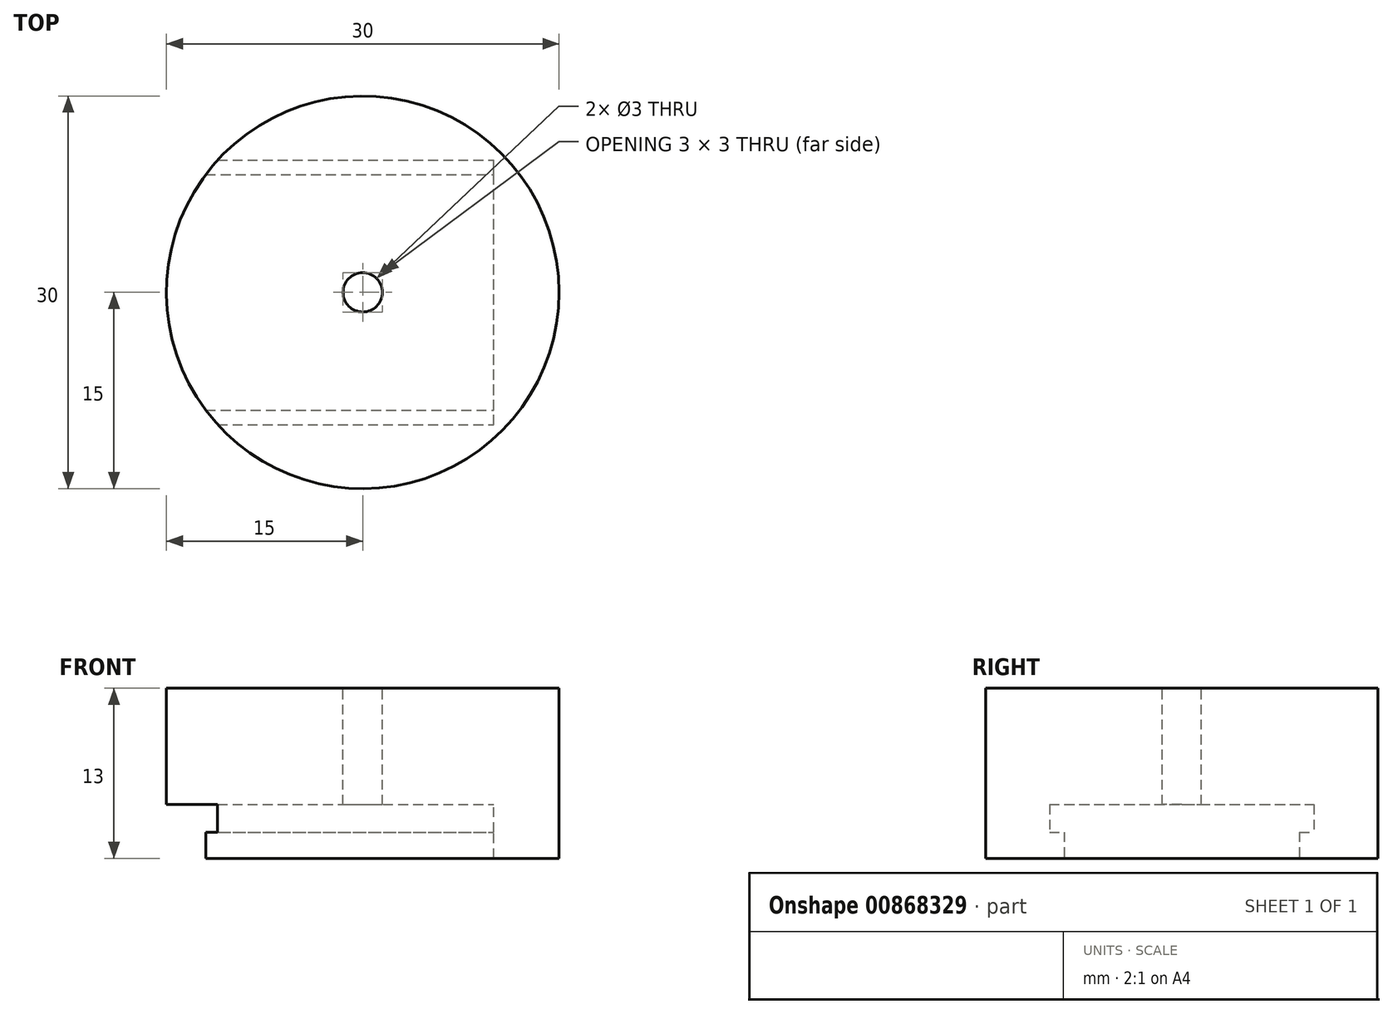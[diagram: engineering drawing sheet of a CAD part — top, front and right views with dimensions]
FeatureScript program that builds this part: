
annotation { "Feature Type Name" : "Feature", "Feature Type Description" : "" }
export const myFeature = defineFeature(function(context is Context, id is Id, definition is map)
    precondition{}
    {
        {
            var Q0;
            Q0=qCreatedBy(makeId("Top.planeOp"),FACE);
            var sketch = newSketch(context, id + "F0", { "sketchPlane" : qUnion([Q0])});
            skCircle(sketch, "E0", {"center": v(0, 0) * mm, "radius": 15 * mm});
            skSolve(sketch);
        }
        {
            var Q0;
            Q0 = qSketchRegion(id + "F0", true);
            extrude(context, id + "F1", {"entities" : qUnion([Q0]), "depth" : 13 * mm, "offsetDistance" : 25 * mm});
        }
        {
            var Q0;
            Q0=qCreatedBy(makeId("Right.planeOp"),FACE);
            var sketch = newSketch(context, id + "F2", { "sketchPlane" : qUnion([Q0])});
            skLineSegment(sketch, "E1.bottom", {"start": v(-9, 0) * mm, "end": v(9, 0) * mm});
            skLineSegment(sketch, "E1.left", {"start": v(-9, 0) * mm, "end": v(-9, 2) * mm});
            skLineSegment(sketch, "E1.right", {"start": v(9, 0) * mm, "end": v(9, 2) * mm});
            skLineSegment(sketch, "E2.bottom", {"start": v(-10.1, 2) * mm, "end": v(-9, 2) * mm});
            skLineSegment(sketch, "E2.top", {"start": v(-10.1, 4.1) * mm, "end": v(10.1, 4.1) * mm});
            skLineSegment(sketch, "E2.left", {"start": v(-10.1, 2) * mm, "end": v(-10.1, 4.1) * mm});
            skLineSegment(sketch, "E2.right", {"start": v(10.1, 2) * mm, "end": v(10.1, 4.1) * mm});
            skLineSegment(sketch, "E3.trimOffspring", {"start": v(9, 2) * mm, "end": v(10.1, 2) * mm});
            skSolve(sketch);
        }
        {
            var Q0;
            Q0 = qSketchRegion(id + "F2", true);
            extrude(context, id + "F3", {"entities" : qUnion([Q0]), "operationType" : NewBodyOperationType.REMOVE, "oppositeDirection" : true, "depth" : 25 * mm, "offsetDistance" : 25 * mm, "hasSecondDirection" : true, "secondDirectionOppositeDirection" : false, "secondDirectionDepth" : 10 * mm});
        }
        {
            var Q0;
            Q0=makeQuery(id+"F1.opExtrude","CAP_FACE",FACE,{"disambiguationData":[OSD([sQuery(id+"F0.wireOp",EDGE,"E0")])],"isStart":false});
            var sketch = newSketch(context, id + "F4", { "sketchPlane" : qUnion([Q0])});
            skCircle(sketch, "E4", {"center": v(0, 0) * mm, "radius": 1.5 * mm});
            skSolve(sketch);
        }
        {
            var Q0;
            Q0 = qSketchRegion(id + "F4", true);
            extrude(context, id + "F5", {"entities" : qUnion([Q0]), "operationType" : NewBodyOperationType.REMOVE, "endBound" : BoundingType.THROUGH_ALL, "oppositeDirection" : true, "depth" : 25 * mm, "offsetDistance" : 25 * mm});
        }
    });
